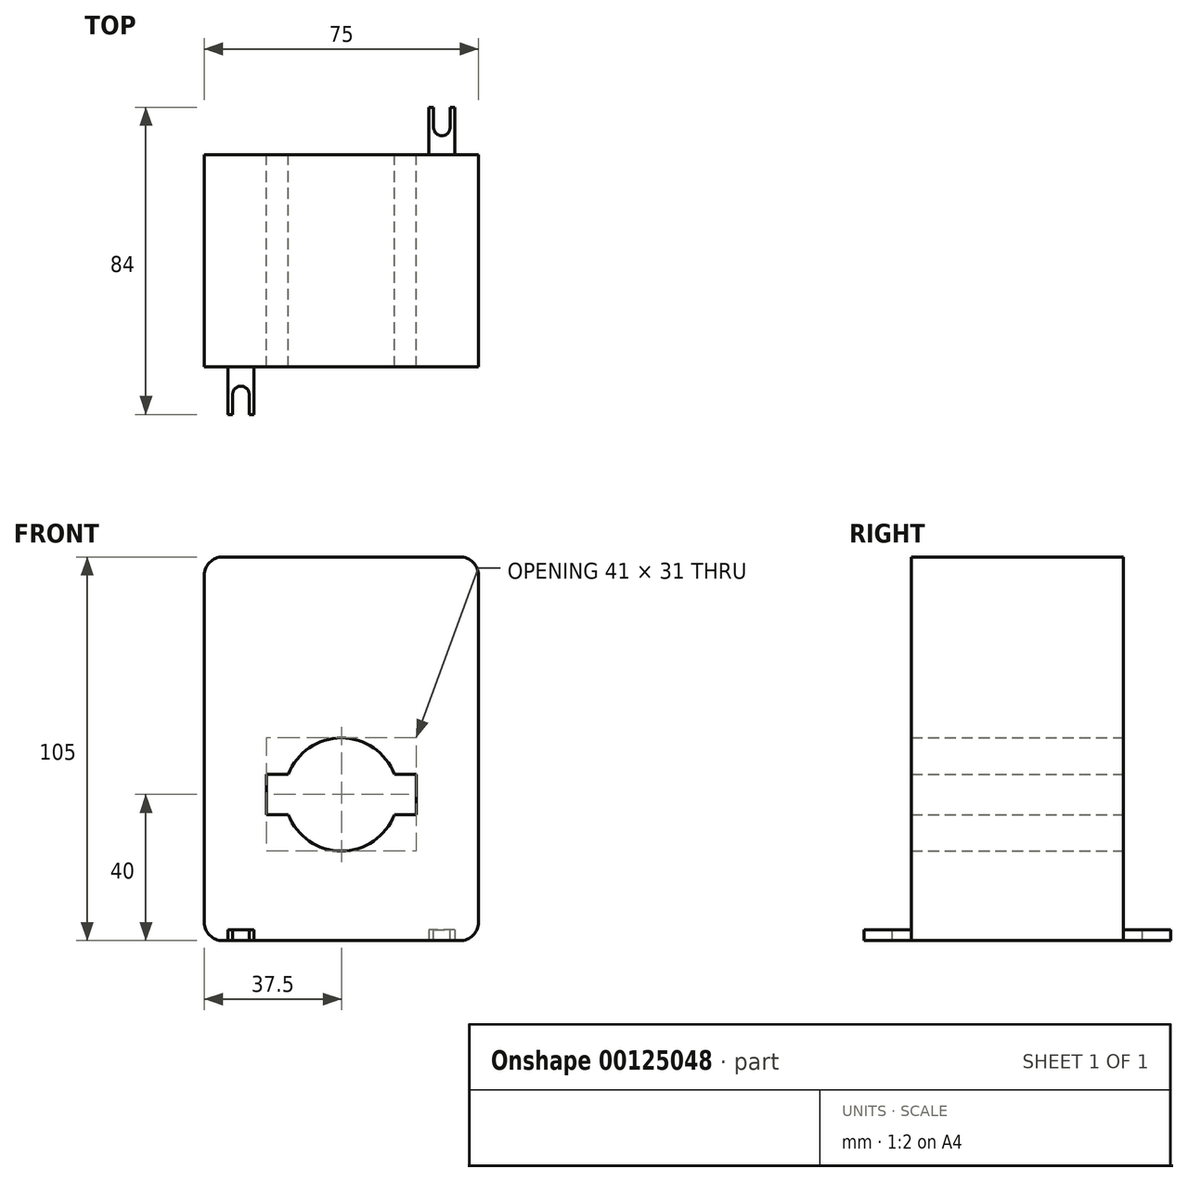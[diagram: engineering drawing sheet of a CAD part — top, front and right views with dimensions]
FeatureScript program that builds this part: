
annotation { "Feature Type Name" : "Feature", "Feature Type Description" : "" }
export const myFeature = defineFeature(function(context is Context, id is Id, definition is map)
    precondition{}
    {
        {
            var Q0;
            Q0=qCreatedBy(makeId("Front.planeOp"),FACE);
            var sketch = newSketch(context, id + "F0", { "sketchPlane" : qUnion([Q0])});
            skLineSegment(sketch, "E0.bottom", {"start": v(37.5, 52.5) * mm, "end": v(-37.5, 52.5) * mm});
            skLineSegment(sketch, "E0.top", {"start": v(37.5, -52.5) * mm, "end": v(-37.5, -52.5) * mm});
            skLineSegment(sketch, "E0.left", {"start": v(37.5, 52.5) * mm, "end": v(37.5, -52.5) * mm});
            skLineSegment(sketch, "E0.right", {"start": v(-37.5, 52.5) * mm, "end": v(-37.5, -52.5) * mm});
            skPoint(sketch, "E1.endSnap0", {"position": v(0, -52.5) * mm});
            skLineSegment(sketch, "E2.bottom", {"start": v(20.5, -18) * mm, "end": v(14.5, -18) * mm});
            skLineSegment(sketch, "E2.top", {"start": v(20.5, -7) * mm, "end": v(14.5, -7) * mm});
            skLineSegment(sketch, "E2.left", {"start": v(20.5, -18) * mm, "end": v(20.5, -7) * mm});
            skLineSegment(sketch, "E2.right", {"start": v(-20.5, -18) * mm, "end": v(-20.5, -7) * mm});
            skPoint(sketch, "E2.middle", {"position": v(0, -12.5) * mm});
            skArc(sketch, "E3", {"start": v(-14.5, -18) * mm, "mid": v(0, -28) * mm, "end": v(14.5, -18) * mm});
            skLineSegment(sketch, "E4.trimOffspring", {"start": v(-14.5, -7) * mm, "end": v(-20.5, -7) * mm});
            skLineSegment(sketch, "E5.trimOffspring", {"start": v(-14.5, -18) * mm, "end": v(-20.5, -18) * mm});
            skArc(sketch, "E6.trimOffspring", {"start": v(14.5, -7) * mm, "mid": v(0, 3) * mm, "end": v(-14.5, -7) * mm});
            skSolve(sketch);
        }
        {
            var Q0;
            Q0=makeQuery(id+"F0.imprint","IMPRINT",FACE,{"disambiguationData":[TD([[makeQuery(id+"F0.imprint","IMPRINT",EDGE,{"derivedFrom":sQuery(id+"F0.wireOp",EDGE,"E0.bottom")}),1.0]])]});
            extrude(context, id + "F1", {"entities" : qUnion([Q0]), "endBound" : BoundingType.SYMMETRIC, "depth" : 58 * mm});
        }
        {
            var Q0;
            Q0=makeQuery(id+"F1.opExtrude","SWEPT_FACE",FACE,{"disambiguationData":[OSD([sQuery(id+"F0.wireOp",EDGE,"E0.top")])]});
            var sketch = newSketch(context, id + "F2", { "sketchPlane" : qUnion([Q0])});
            skLineSegment(sketch, "E7.bottom", {"start": v(-24, 29) * mm, "end": v(-31, 29) * mm});
            skLineSegment(sketch, "E7.top", {"start": v(-24, 42) * mm, "end": v(-31, 42) * mm});
            skLineSegment(sketch, "E7.left", {"start": v(-24, 29) * mm, "end": v(-24, 42) * mm});
            skLineSegment(sketch, "E7.right", {"start": v(-31, 29) * mm, "end": v(-31, 42) * mm});
            skLineSegment(sketch, "E8.bottom", {"start": v(31, -29) * mm, "end": v(24, -29) * mm});
            skLineSegment(sketch, "E8.top", {"start": v(31, -42) * mm, "end": v(24, -42) * mm});
            skLineSegment(sketch, "E8.left", {"start": v(31, -29) * mm, "end": v(31, -42) * mm});
            skLineSegment(sketch, "E8.right", {"start": v(24, -29) * mm, "end": v(24, -42) * mm});
            skSolve(sketch);
        }
        {
            var Q0;
            Q0=makeQuery(id+"F2.imprint","IMPRINT",FACE,{"disambiguationData":[TD([[makeQuery(id+"F2.imprint","IMPRINT",EDGE,{"derivedFrom":sQuery(id+"F2.wireOp",EDGE,"E7.bottom")}),-1.0]])]});
            var Q1;
            Q1=makeQuery(id+"F2.imprint","IMPRINT",FACE,{"disambiguationData":[TD([[makeQuery(id+"F2.imprint","IMPRINT",EDGE,{"derivedFrom":sQuery(id+"F2.wireOp",EDGE,"E8.bottom")}),1.0]])]});
            extrude(context, id + "F3", {"entities" : qUnion([Q0, Q1]), "operationType" : NewBodyOperationType.ADD, "oppositeDirection" : true, "depth" : 3 * mm});
        }
        {
            var Q0;
            Q0=makeQuery(id+"F3.opExtrude","CAP_FACE",FACE,{"disambiguationData":[OSD([sQuery(id+"F2.wireOp",EDGE,"E7.bottom"),sQuery(id+"F2.wireOp",EDGE,"E7.top"),sQuery(id+"F2.wireOp",EDGE,"E7.left"),sQuery(id+"F2.wireOp",EDGE,"E7.right")])],"isStart":false});
            var sketch = newSketch(context, id + "F4", { "sketchPlane" : qUnion([Q0])});
            skArc(sketch, "E9", {"start": v(-25.25, -36.5) * mm, "mid": v(-27.5, -34.25) * mm, "end": v(-29.75, -36.5) * mm});
            skLineSegment(sketch, "E10", {"start": v(-29.75, -36.5) * mm, "end": v(-29.75, -42) * mm});
            skLineSegment(sketch, "E11.MirrorCS", {"start": v(-25.25, -36.5) * mm, "end": v(-25.25, -42) * mm});
            skSolve(sketch);
        }
        {
            var Q0;
            Q0=makeQuery(id+"F3.opExtrude","CAP_FACE",FACE,{"disambiguationData":[OSD([sQuery(id+"F2.wireOp",EDGE,"E8.bottom"),sQuery(id+"F2.wireOp",EDGE,"E8.top"),sQuery(id+"F2.wireOp",EDGE,"E8.left"),sQuery(id+"F2.wireOp",EDGE,"E8.right")])],"isStart":false});
            var sketch = newSketch(context, id + "F5", { "sketchPlane" : qUnion([Q0])});
            skArc(sketch, "E12", {"start": v(25.25, 36.5) * mm, "mid": v(27.5, 34.25) * mm, "end": v(29.75, 36.5) * mm});
            skPoint(sketch, "E12.centerSnap0", {"position": v(27.5, 42) * mm});
            skLineSegment(sketch, "E13", {"start": v(25.25, 36.5) * mm, "end": v(25.25, 42) * mm});
            skLineSegment(sketch, "E14.MirrorCS", {"start": v(29.75, 36.5) * mm, "end": v(29.75, 42) * mm});
            skSolve(sketch);
        }
        {
            var Q0;
            Q0=makeQuery(id+"F5.imprint","IMPRINT",FACE,{"disambiguationData":[TD([[makeQuery(id+"F5.imprint","IMPRINT",EDGE,{"derivedFrom":sQuery(id+"F5.wireOp",EDGE,"E12")}),1.0]])]});
            var Q1;
            Q1=makeQuery(id+"F4.imprint","IMPRINT",FACE,{"disambiguationData":[TD([[makeQuery(id+"F4.imprint","IMPRINT",EDGE,{"derivedFrom":sQuery(id+"F4.wireOp",EDGE,"E9")}),1.0]])]});
            extrude(context, id + "F6", {"entities" : qUnion([Q0, Q1]), "operationType" : NewBodyOperationType.REMOVE, "oppositeDirection" : true, "depth" : 25 * mm});
        }
        {
            var Q0;
            Q0=makeQuery(id+"F1.opExtrude","SWEPT_EDGE",EDGE,{"disambiguationData":[OSD([sQuery(id+"F0.wireOp",EDGE,"E0.top"),sQuery(id+"F0.wireOp",EDGE,"E0.right")])]});
            var Q1;
            Q1=makeQuery(id+"F1.opExtrude","SWEPT_EDGE",EDGE,{"disambiguationData":[OSD([sQuery(id+"F0.wireOp",EDGE,"E0.top"),sQuery(id+"F0.wireOp",EDGE,"E0.left")])]});
            var Q2;
            Q2=makeQuery(id+"F1.opExtrude","SWEPT_EDGE",EDGE,{"disambiguationData":[OSD([sQuery(id+"F0.wireOp",EDGE,"E0.bottom"),sQuery(id+"F0.wireOp",EDGE,"E0.left")])]});
            var Q3;
            Q3=makeQuery(id+"F1.opExtrude","SWEPT_EDGE",EDGE,{"disambiguationData":[OSD([sQuery(id+"F0.wireOp",EDGE,"E0.bottom"),sQuery(id+"F0.wireOp",EDGE,"E0.right")])]});
            fillet(context, id + "F7", {"entities" : qUnion([Q0, Q1, Q2, Q3]), "radius" : 5 * mm, "tangentPropagation" : true, "allowEdgeOverflow" : false});
        }
    });
